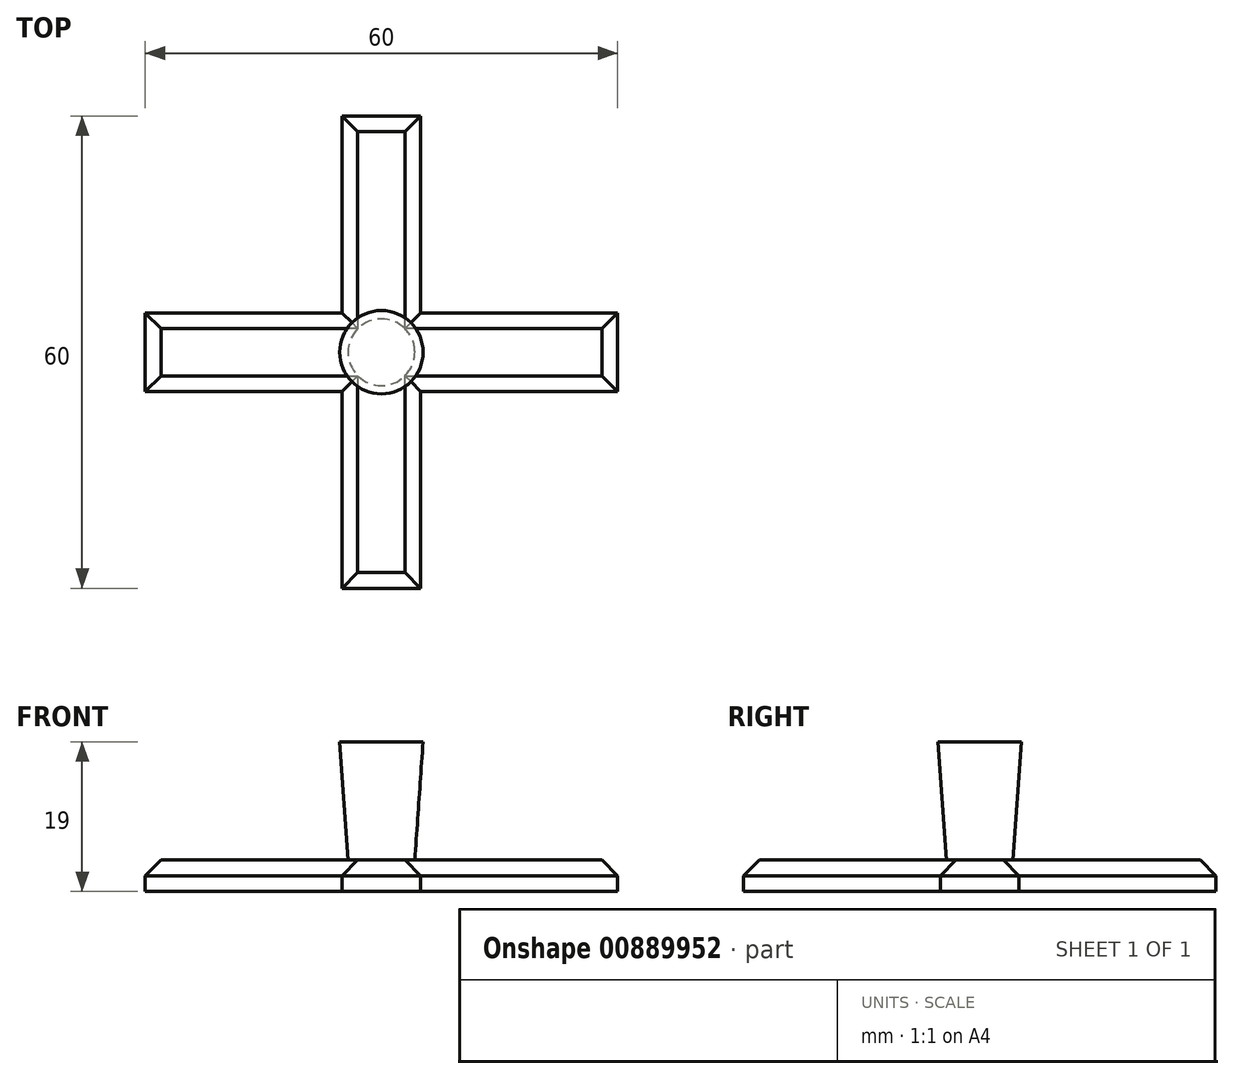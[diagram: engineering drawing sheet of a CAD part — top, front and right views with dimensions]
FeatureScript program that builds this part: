
annotation { "Feature Type Name" : "Feature", "Feature Type Description" : "" }
export const myFeature = defineFeature(function(context is Context, id is Id, definition is map)
    precondition{}
    {
        {
            var Q0;
            Q0=qCreatedBy(makeId("Top.planeOp"),FACE);
            var sketch = newSketch(context, id + "F0", { "sketchPlane" : qUnion([Q0])});
            skLineSegment(sketch, "E0", {"start": v(0, 0) * mm, "end": v(30, 0) * mm, "construction": true});
            skLineSegment(sketch, "E1", {"start": v(0, 0) * mm, "end": v(0, -30) * mm, "construction": true});
            skLineSegment(sketch, "E2.0", {"start": v(5, -5) * mm, "end": v(30, -5) * mm});
            skLineSegment(sketch, "E2.1", {"start": v(5, -5) * mm, "end": v(5, -30) * mm});
            skLineSegment(sketch, "E3.MirrorCS", {"start": v(-5, -5) * mm, "end": v(-5, -30) * mm});
            skLineSegment(sketch, "E4.MirrorCS", {"start": v(-5, -5) * mm, "end": v(-30, -5) * mm});
            skLineSegment(sketch, "E5.MirrorCS", {"start": v(-5, 5) * mm, "end": v(-30, 5) * mm});
            skLineSegment(sketch, "E6.MirrorCS", {"start": v(-5, 5) * mm, "end": v(-5, 30) * mm});
            skLineSegment(sketch, "E7.MirrorCS", {"start": v(5, 5) * mm, "end": v(30, 5) * mm});
            skLineSegment(sketch, "E8.MirrorCS", {"start": v(5, 5) * mm, "end": v(5, 30) * mm});
            skLineSegment(sketch, "E9", {"start": v(-5, 30) * mm, "end": v(5, 30) * mm});
            skLineSegment(sketch, "E10", {"start": v(30, 5) * mm, "end": v(30, -5) * mm});
            skLineSegment(sketch, "E11", {"start": v(5, -30) * mm, "end": v(-5, -30) * mm});
            skLineSegment(sketch, "E12", {"start": v(-30, -5) * mm, "end": v(-30, 5) * mm});
            skSolve(sketch);
        }
        {
            var Q0;
            Q0 = qSketchRegion(id + "F0", true);
            extrude(context, id + "F1", {"entities" : qUnion([Q0]), "depth" : 4 * mm, "offsetDistance" : 25 * mm});
        }
        {
            var Q0;
            Q0=makeQuery(id+"F1.opExtrude","CAP_EDGE",EDGE,{"disambiguationData":[OSD([sQuery(id+"F0.wireOp",EDGE,"E6.MirrorCS")])],"isStart":false});
            var Q1;
            Q1=makeQuery(id+"F1.opExtrude","CAP_EDGE",EDGE,{"disambiguationData":[OSD([sQuery(id+"F0.wireOp",EDGE,"E9")])],"isStart":false});
            var Q2;
            Q2=makeQuery(id+"F1.opExtrude","CAP_EDGE",EDGE,{"disambiguationData":[OSD([sQuery(id+"F0.wireOp",EDGE,"E8.MirrorCS")])],"isStart":false});
            var Q3;
            Q3=makeQuery(id+"F1.opExtrude","CAP_EDGE",EDGE,{"disambiguationData":[OSD([sQuery(id+"F0.wireOp",EDGE,"E5.MirrorCS")])],"isStart":false});
            var Q4;
            Q4=makeQuery(id+"F1.opExtrude","CAP_EDGE",EDGE,{"disambiguationData":[OSD([sQuery(id+"F0.wireOp",EDGE,"E4.MirrorCS")])],"isStart":false});
            var Q5;
            Q5=makeQuery(id+"F1.opExtrude","CAP_EDGE",EDGE,{"disambiguationData":[OSD([sQuery(id+"F0.wireOp",EDGE,"E12")])],"isStart":false});
            var Q6;
            Q6=makeQuery(id+"F1.opExtrude","CAP_EDGE",EDGE,{"disambiguationData":[OSD([sQuery(id+"F0.wireOp",EDGE,"E3.MirrorCS")])],"isStart":false});
            var Q7;
            Q7=makeQuery(id+"F1.opExtrude","CAP_EDGE",EDGE,{"disambiguationData":[OSD([sQuery(id+"F0.wireOp",EDGE,"E11")])],"isStart":false});
            var Q8;
            Q8=makeQuery(id+"F1.opExtrude","CAP_EDGE",EDGE,{"disambiguationData":[OSD([sQuery(id+"F0.wireOp",EDGE,"E2.1")])],"isStart":false});
            var Q9;
            Q9=makeQuery(id+"F1.opExtrude","CAP_EDGE",EDGE,{"disambiguationData":[OSD([sQuery(id+"F0.wireOp",EDGE,"E2.0")])],"isStart":false});
            var Q10;
            Q10=makeQuery(id+"F1.opExtrude","CAP_EDGE",EDGE,{"disambiguationData":[OSD([sQuery(id+"F0.wireOp",EDGE,"E7.MirrorCS")])],"isStart":false});
            var Q11;
            Q11=makeQuery(id+"F1.opExtrude","CAP_EDGE",EDGE,{"disambiguationData":[OSD([sQuery(id+"F0.wireOp",EDGE,"E10")])],"isStart":false});
            chamfer(context, id + "F2", {"entities" : qUnion([Q0, Q1, Q2, Q3, Q4, Q5, Q6, Q7, Q8, Q9, Q10, Q11]), "width" : 2 * mm, "tangentPropagation" : true});
        }
        {
            var Q0;
            Q0=makeQuery(id+"F1.opExtrude","CAP_FACE",FACE,{"disambiguationData":[OSD([sQuery(id+"F0.wireOp",EDGE,"E2.0"),sQuery(id+"F0.wireOp",EDGE,"E2.1"),sQuery(id+"F0.wireOp",EDGE,"E3.MirrorCS"),sQuery(id+"F0.wireOp",EDGE,"E4.MirrorCS"),sQuery(id+"F0.wireOp",EDGE,"E5.MirrorCS"),sQuery(id+"F0.wireOp",EDGE,"E6.MirrorCS"),sQuery(id+"F0.wireOp",EDGE,"E7.MirrorCS"),sQuery(id+"F0.wireOp",EDGE,"E8.MirrorCS"),sQuery(id+"F0.wireOp",EDGE,"E9"),sQuery(id+"F0.wireOp",EDGE,"E10"),sQuery(id+"F0.wireOp",EDGE,"E11"),sQuery(id+"F0.wireOp",EDGE,"E12")])],"isStart":false});
            var sketch = newSketch(context, id + "F3", { "sketchPlane" : qUnion([Q0])});
            skCircle(sketch, "E13", {"center": v(0, 0) * mm, "radius": 4.24 * mm});
            skSolve(sketch);
        }
        {
            var Q0;
            {var subQ0=sQuery(id+"F3.wireOp",EDGE,"E13");var subQ1=sQuery(id+"F0.wireOp",EDGE,"E8.MirrorCS");var subQ2=sQuery(id+"F0.wireOp",EDGE,"E7.MirrorCS");var subQ3=sQuery(id+"F0.wireOp",EDGE,"E6.MirrorCS");var subQ4=sQuery(id+"F0.wireOp",EDGE,"E5.MirrorCS");var subQ5=sQuery(id+"F0.wireOp",EDGE,"E4.MirrorCS");var subQ6=sQuery(id+"F0.wireOp",EDGE,"E3.MirrorCS");var subQ7=sQuery(id+"F0.wireOp",EDGE,"E2.1");var subQ8=sQuery(id+"F0.wireOp",EDGE,"E2.0");var subQ9=makeQuery(id+"F1.opExtrude","CAP_FACE",FACE,{"disambiguationData":[OSD([subQ8,subQ7,subQ6,subQ5,subQ4,subQ3,subQ2,subQ1,sQuery(id+"F0.wireOp",EDGE,"E9"),sQuery(id+"F0.wireOp",EDGE,"E10"),sQuery(id+"F0.wireOp",EDGE,"E11"),sQuery(id+"F0.wireOp",EDGE,"E12")])],"isStart":false});var subQ10=makeQuery(id+"F3.imprint","INTERSECT",VERTEX,{"derivedFrom":[makeQuery(id+"F2.opChamfer","BLEND_EDGE",EDGE,{"blendedFrom":[makeQuery(id+"F1.opExtrude","CAP_EDGE",EDGE,{"disambiguationData":[OSD([subQ4])],"isStart":false}),subQ9],"blendedInto":[subQ9]}),makeQuery(id+"F2.opChamfer","BLEND_EDGE",EDGE,{"blendedFrom":[makeQuery(id+"F1.opExtrude","CAP_EDGE",EDGE,{"disambiguationData":[OSD([subQ3])],"isStart":false}),subQ9],"blendedInto":[subQ9]}),subQ0]});Q0=makeQuery(id+"F3.imprint","IMPRINT",FACE,{"disambiguationData":[TD([[makeQuery(id+"F3.imprint","IMPRINT",EDGE,{"disambiguationData":[TD([[subQ10,1.0]])],"derivedFrom":subQ0}),1.0]])]});}
            extrude(context, id + "F4", {"entities" : qUnion([Q0]), "operationType" : NewBodyOperationType.ADD, "depth" : 15 * mm, "offsetDistance" : 25 * mm, "hasDraft" : true, "draftAngle" : 4 * degree});
        }
    });
